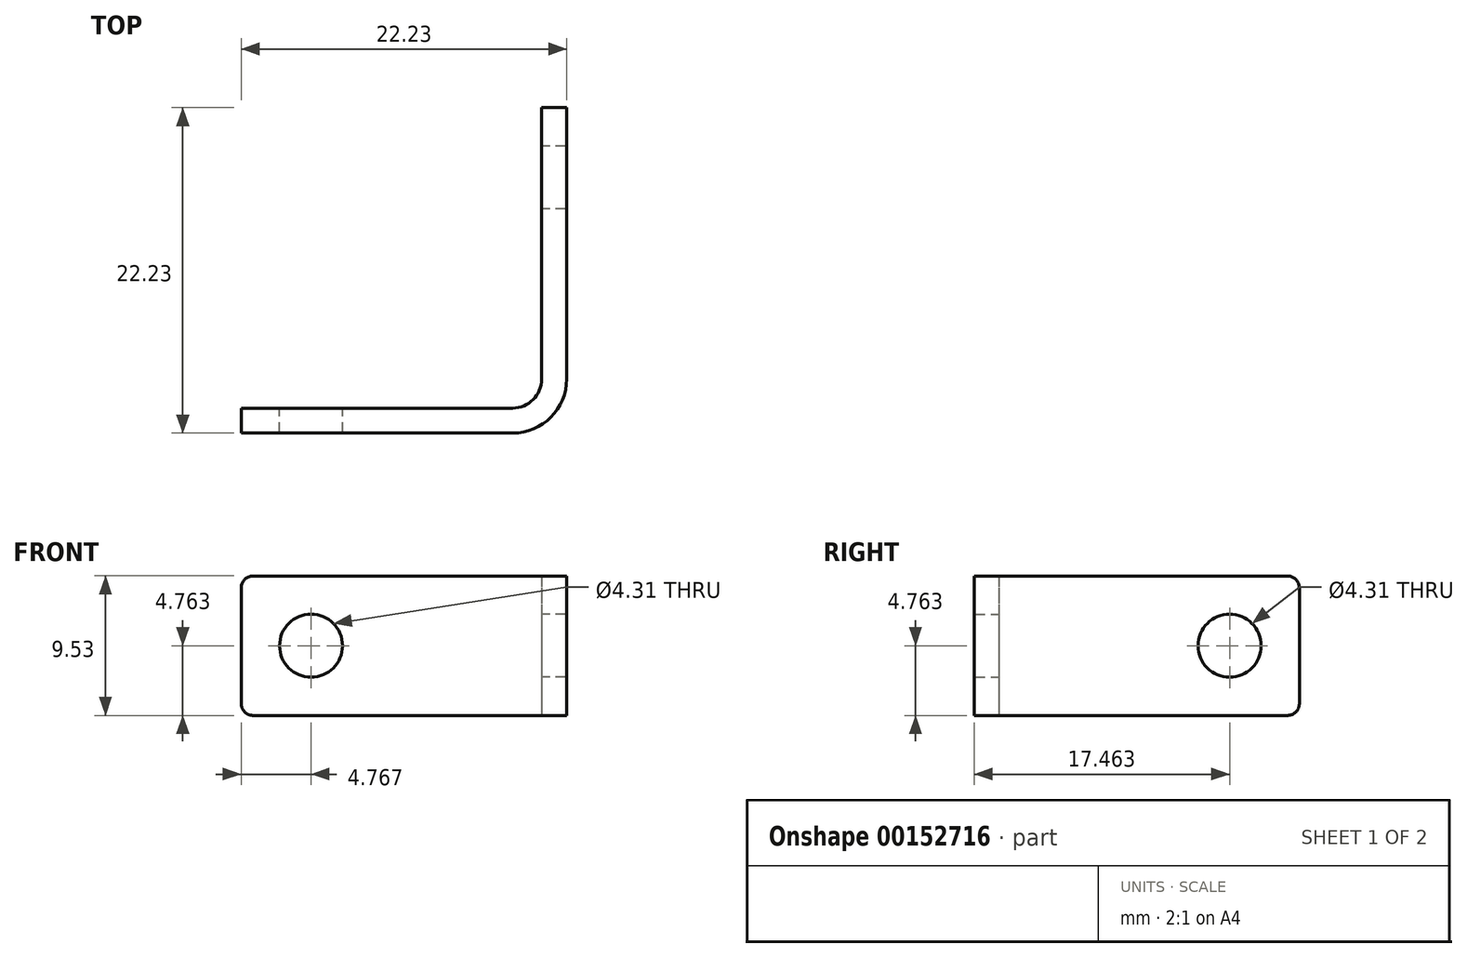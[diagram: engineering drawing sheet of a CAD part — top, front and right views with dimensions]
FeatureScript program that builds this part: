
annotation { "Feature Type Name" : "Feature", "Feature Type Description" : "" }
export const myFeature = defineFeature(function(context is Context, id is Id, definition is map)
    precondition{}
    {
        {
            var Q0;
            Q0=qCreatedBy(makeId("Top.planeOp"),FACE);
            var sketch = newSketch(context, id + "F0", { "sketchPlane" : qUnion([Q0])});
            skLineSegment(sketch, "E0.bottom", {"start": v(0, 0) * mm, "end": v(-20.52, 0) * mm});
            skLineSegment(sketch, "E0.top", {"start": v(1.7, -1.7) * mm, "end": v(-20.52, -1.7) * mm});
            skLineSegment(sketch, "E1.right", {"start": v(-20.52, -1.7) * mm, "end": v(-20.52, 0) * mm});
            skLineSegment(sketch, "E2.top", {"start": v(0, 20.52) * mm, "end": v(1.7, 20.52) * mm});
            skLineSegment(sketch, "E2.left", {"start": v(0, 0) * mm, "end": v(0, 20.52) * mm});
            skLineSegment(sketch, "E2.right", {"start": v(1.7, -1.7) * mm, "end": v(1.7, 20.52) * mm});
            skSolve(sketch);
        }
        {
            var Q0;
            Q0=qSketchRegion(id+"F0",true);
            extrude(context, id + "F1", {"entities" : qUnion([Q0]), "depth" : 9.52 * mm});
        }
        {
            var Q0;
            Q0=makeQuery(id+"F1.opExtrude","SWEPT_EDGE",EDGE,{"disambiguationData":[OSD([sQuery(id+"F0.wireOp",EDGE,"E0.bottom"),sQuery(id+"F0.wireOp",EDGE,"E2.left")])]});
            fillet(context, id + "F2", {"entities" : qUnion([Q0]), "radius" : 1.98 * mm, "tangentPropagation" : true, "allowEdgeOverflow" : false});
        }
        {
            var Q0;
            Q0=makeQuery(id+"F1.opExtrude","SWEPT_EDGE",EDGE,{"disambiguationData":[OSD([sQuery(id+"F0.wireOp",EDGE,"E0.top"),sQuery(id+"F0.wireOp",EDGE,"E2.right")])]});
            fillet(context, id + "F3", {"entities" : qUnion([Q0]), "radius" : 3.7 * mm, "tangentPropagation" : true, "allowEdgeOverflow" : false});
        }
        {
            var Q0;
            Q0=makeQuery(id+"F1.opExtrude","SWEPT_FACE",FACE,{"disambiguationData":[OSD([sQuery(id+"F0.wireOp",EDGE,"E0.bottom")])]});
            var sketch = newSketch(context, id + "F4", { "sketchPlane" : qUnion([Q0])});
            skLineSegment(sketch, "E3.bottom", {"start": v(20.52, 4.76) * mm, "end": v(15.75, 4.76) * mm, "construction": true});
            skLineSegment(sketch, "E3.top", {"start": v(20.52, 9.53) * mm, "end": v(15.75, 9.53) * mm, "construction": true});
            skLineSegment(sketch, "E3.left", {"start": v(20.52, 4.76) * mm, "end": v(20.52, 9.53) * mm, "construction": true});
            skLineSegment(sketch, "E3.right", {"start": v(15.75, 4.76) * mm, "end": v(15.75, 9.53) * mm, "construction": true});
            skCircle(sketch, "E4", {"center": v(15.75, 4.76) * mm, "radius": 2.15 * mm});
            skSolve(sketch);
        }
        {
            var Q0;
            Q0 = qSketchRegion(id + "F4", true);
            var Q1;
            Q1=makeQuery(id+"F1.opExtrude","SWEPT_FACE",FACE,{"disambiguationData":[OSD([sQuery(id+"F0.wireOp",EDGE,"E0.top")])]});
            extrude(context, id + "F5", {"entities" : qUnion([Q0]), "operationType" : NewBodyOperationType.REMOVE, "endBound" : BoundingType.UP_TO_SURFACE, "oppositeDirection" : true, "endBoundEntityFace" : qUnion([Q1]), "depth" : 25.4 * mm});
        }
        {
            var Q0;
            Q0=makeQuery(id+"F1.opExtrude","SWEPT_FACE",FACE,{"disambiguationData":[OSD([sQuery(id+"F0.wireOp",EDGE,"E2.left")])]});
            var sketch = newSketch(context, id + "F6", { "sketchPlane" : qUnion([Q0])});
            skLineSegment(sketch, "E5.bottom", {"start": v(-20.52, 4.76) * mm, "end": v(-15.75, 4.76) * mm, "construction": true});
            skLineSegment(sketch, "E5.top", {"start": v(-20.52, 9.53) * mm, "end": v(-15.75, 9.53) * mm, "construction": true});
            skLineSegment(sketch, "E5.left", {"start": v(-20.52, 4.76) * mm, "end": v(-20.52, 9.53) * mm, "construction": true});
            skLineSegment(sketch, "E5.right", {"start": v(-15.75, 4.76) * mm, "end": v(-15.75, 9.53) * mm, "construction": true});
            skCircle(sketch, "E6", {"center": v(-15.75, 4.76) * mm, "radius": 2.15 * mm});
            skSolve(sketch);
        }
        {
            var Q0;
            Q0 = qSketchRegion(id + "F6", true);
            var Q1;
            Q1=makeQuery(id+"F1.opExtrude","SWEPT_FACE",FACE,{"disambiguationData":[OSD([sQuery(id+"F0.wireOp",EDGE,"E2.right")])]});
            extrude(context, id + "F7", {"entities" : qUnion([Q0]), "operationType" : NewBodyOperationType.REMOVE, "endBound" : BoundingType.UP_TO_SURFACE, "oppositeDirection" : true, "endBoundEntityFace" : qUnion([Q1]), "depth" : 25.4 * mm});
        }
        {
            var Q0;
            Q0=makeQuery(id+"F1.opExtrude","CAP_EDGE",EDGE,{"disambiguationData":[OSD([sQuery(id+"F0.wireOp",EDGE,"E2.top")])],"isStart":true});
            var Q1;
            Q1=makeQuery(id+"F1.opExtrude","CAP_EDGE",EDGE,{"disambiguationData":[OSD([sQuery(id+"F0.wireOp",EDGE,"E2.top")])],"isStart":false});
            var Q2;
            Q2=makeQuery(id+"F1.opExtrude","CAP_EDGE",EDGE,{"disambiguationData":[OSD([sQuery(id+"F0.wireOp",EDGE,"E1.right")])],"isStart":false});
            var Q3;
            Q3=makeQuery(id+"F1.opExtrude","CAP_EDGE",EDGE,{"disambiguationData":[OSD([sQuery(id+"F0.wireOp",EDGE,"E1.right")])],"isStart":true});
            fillet(context, id + "F8", {"entities" : qUnion([Q0, Q1, Q2, Q3]), "radius" : 0.8 * mm, "tangentPropagation" : true, "allowEdgeOverflow" : false});
        }
    });
